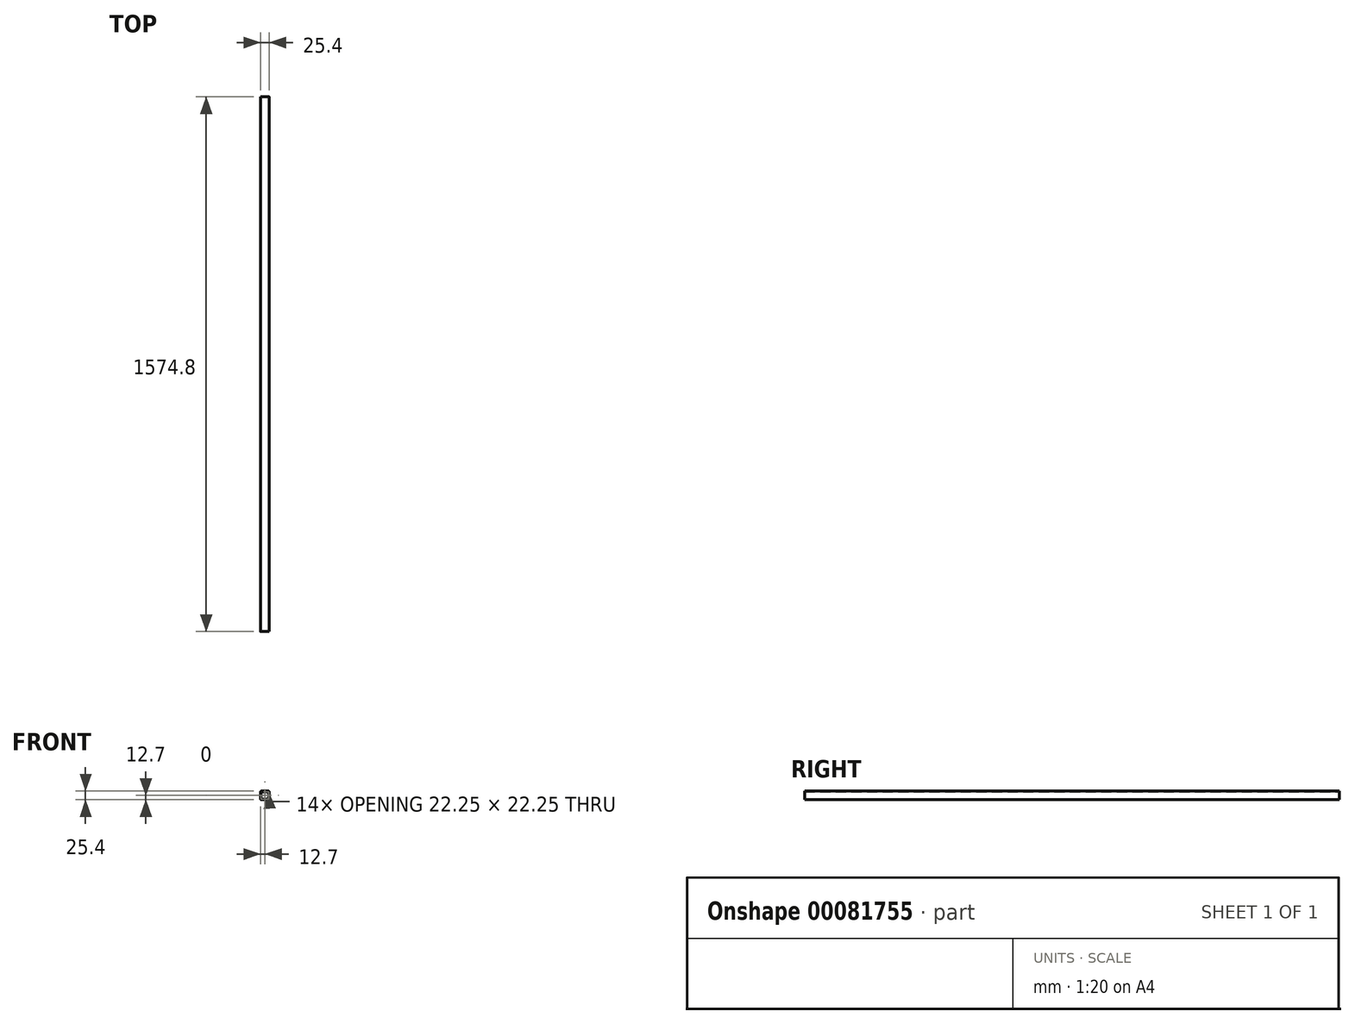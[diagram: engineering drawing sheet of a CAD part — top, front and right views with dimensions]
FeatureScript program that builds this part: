
annotation { "Feature Type Name" : "Feature", "Feature Type Description" : "" }
export const myFeature = defineFeature(function(context is Context, id is Id, definition is map)
    precondition{}
    {
        {
            var Q0;
            Q0=qCreatedBy(makeId("Front.planeOp"),FACE);
            var sketch = newSketch(context, id + "F0", { "sketchPlane" : qUnion([Q0])});
            skLineSegment(sketch, "E0.bottom", {"start": v(-10.62, -12.7) * mm, "end": v(10.62, -12.7) * mm});
            skLineSegment(sketch, "E0.top", {"start": v(-10.62, 12.7) * mm, "end": v(10.62, 12.7) * mm});
            skLineSegment(sketch, "E0.left", {"start": v(-12.7, -10.62) * mm, "end": v(-12.7, 10.62) * mm});
            skLineSegment(sketch, "E0.right", {"start": v(12.7, -10.62) * mm, "end": v(12.7, 10.62) * mm});
            skPoint(sketch, "E0.middle", {"position": v(0, 0) * mm});
            skLineSegment(sketch, "E1.bottom", {"start": v(10.62, -11.13) * mm, "end": v(-10.62, -11.13) * mm});
            skLineSegment(sketch, "E1.top", {"start": v(10.62, 11.13) * mm, "end": v(-10.62, 11.13) * mm});
            skLineSegment(sketch, "E1.left", {"start": v(11.13, -10.62) * mm, "end": v(11.13, 10.62) * mm});
            skLineSegment(sketch, "E1.right", {"start": v(-11.13, -10.62) * mm, "end": v(-11.13, 10.62) * mm});
            skPoint(sketch, "E2.visualSharp", {"position": v(-11.13, 11.13) * mm});
            skArc(sketch, "E2.filletArc", {"start": v(-10.74, 11.13) * mm, "mid": v(-11.01, 11.01) * mm, "end": v(-11.13, 10.74) * mm});
            skPoint(sketch, "E3.visualSharp", {"position": v(11.13, 11.13) * mm});
            skArc(sketch, "E3.filletArc", {"start": v(11.13, 10.62) * mm, "mid": v(10.98, 10.98) * mm, "end": v(10.62, 11.13) * mm});
            skPoint(sketch, "E4.visualSharp", {"position": v(-11.13, -11.13) * mm});
            skArc(sketch, "E4.filletArc", {"start": v(-11.13, -10.62) * mm, "mid": v(-10.98, -10.98) * mm, "end": v(-10.62, -11.13) * mm});
            skPoint(sketch, "E5.visualSharp", {"position": v(11.13, -11.13) * mm});
            skArc(sketch, "E5.filletArc", {"start": v(10.62, -11.13) * mm, "mid": v(10.98, -10.98) * mm, "end": v(11.13, -10.62) * mm});
            skArc(sketch, "E6.filletArc", {"start": v(-10.62, 11.13) * mm, "mid": v(-10.98, 10.98) * mm, "end": v(-11.13, 10.62) * mm});
            skPoint(sketch, "E7.visualSharp", {"position": v(12.7, 12.7) * mm});
            skArc(sketch, "E7.filletArc", {"start": v(12.7, 10.62) * mm, "mid": v(12.09, 12.09) * mm, "end": v(10.62, 12.7) * mm});
            skPoint(sketch, "E8.visualSharp", {"position": v(12.7, -12.7) * mm});
            skArc(sketch, "E8.filletArc", {"start": v(10.62, -12.7) * mm, "mid": v(12.09, -12.09) * mm, "end": v(12.7, -10.62) * mm});
            skPoint(sketch, "E9.visualSharp", {"position": v(-12.7, -12.7) * mm});
            skArc(sketch, "E9.filletArc", {"start": v(-12.7, -10.62) * mm, "mid": v(-12.09, -12.09) * mm, "end": v(-10.62, -12.7) * mm});
            skPoint(sketch, "E10.visualSharp", {"position": v(-12.7, 12.7) * mm});
            skArc(sketch, "E10.filletArc", {"start": v(-10.62, 12.7) * mm, "mid": v(-12.09, 12.09) * mm, "end": v(-12.7, 10.62) * mm});
            skSolve(sketch);
        }
        {
            var Q0;
            Q0 = qSketchRegion(id + "F0", true);
            extrude(context, id + "F1", {"entities" : qUnion([Q0]), "depth" : 1574.8 * mm, "offsetDistance" : 25.4 * mm});
        }
    });
